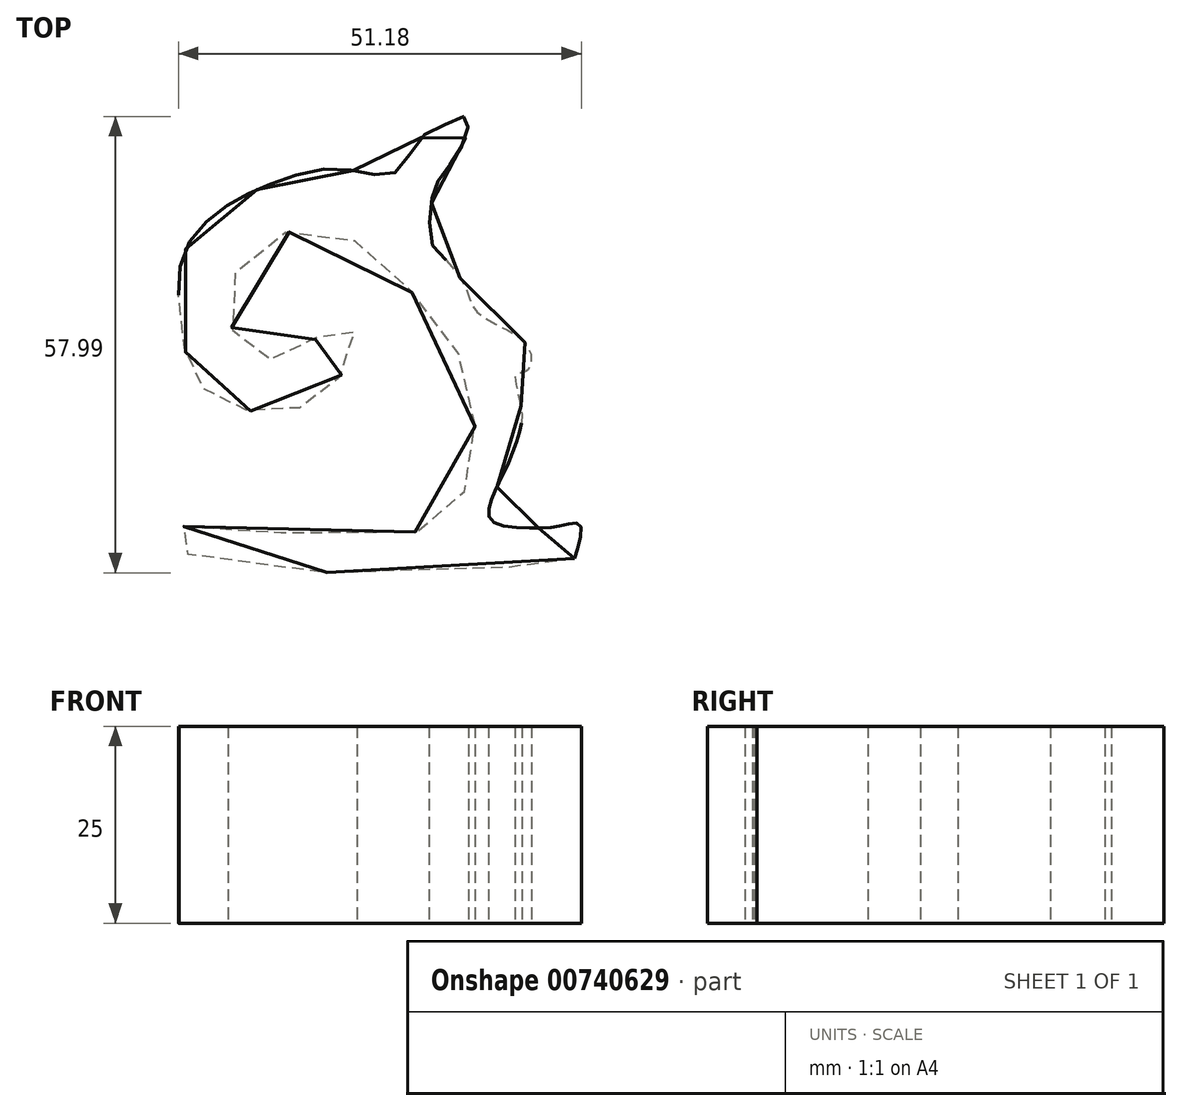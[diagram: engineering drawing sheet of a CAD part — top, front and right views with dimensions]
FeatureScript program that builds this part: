
annotation { "Feature Type Name" : "Feature", "Feature Type Description" : "" }
export const myFeature = defineFeature(function(context is Context, id is Id, definition is map)
    precondition{}
    {
        {
            var Q0;
            Q0=qCreatedBy(makeId("Top.planeOp"),FACE);
            var sketch = newSketch(context, id + "F0", { "sketchPlane" : qUnion([Q0])});
            skFitSpline(sketch, "E0", {"points": [v(124.73, -290.05) * mm, v(123.75, -290.64) * mm, v(75.1, -289.1) * mm, v(74.92, -286.08) * mm, v(74.93, -286.05) * mm, v(75.1, -285.97) * mm, v(106.34, -286.28) * mm, v(111.08, -279.96) * mm, v(111.72, -268.27) * mm, v(104.15, -256.29) * mm, v(94.37, -248.71) * mm, v(83.66, -250.92) * mm, v(80.82, -259.12) * mm, v(83.65, -263.84) * mm, v(89.62, -264.15) * mm, v(94.66, -260.06) * mm, v(97.12, -262.5) * mm, v(93.71, -268.24) * mm, v(89.3, -271.07) * mm, v(82.39, -271.07) * mm, v(77.67, -268.55) * mm, v(75.47, -264.46) * mm, v(74.53, -258.17) * mm, v(74.97, -251.62) * mm, v(78.25, -247.03) * mm, v(82.7, -244.02) * mm, v(87.1, -242.13) * mm, v(93.4, -240.56) * mm, v(98.75, -241.19) * mm, v(102.2, -240.87) * mm, v(105.04, -236.78) * mm, v(108.78, -234.71) * mm, v(111.01, -233.95) * mm, v(111.01, -236.16) * mm, v(109.44, -239.3) * mm, v(107.34, -242.18) * mm, v(106.55, -244.93) * mm, v(106.55, -249.91) * mm, v(108.65, -252.4) * mm, v(111.14, -256.2) * mm, v(112.58, -258.96) * mm, v(118.88, -263.2) * mm, v(118.56, -266.35) * mm, v(117.3, -266.67) * mm, v(117.93, -270.76) * mm, v(117.62, -274.53) * mm, v(115.73, -279.25) * mm, v(114.15, -282.68) * mm, v(114.16, -285.22) * mm, v(119.5, -286.17) * mm, v(123.28, -285.85) * mm, v(125.48, -285.85) * mm, v(124.73, -290.05) * mm]});
            skSolve(sketch);
        }
        {
            var Q0;
            Q0=makeQuery(id+"F0.imprint","IMPRINT",FACE,{"disambiguationData":[TD([[makeQuery(id+"F0.imprint","IMPRINT",EDGE,{"derivedFrom":sQuery(id+"F0.wireOp",EDGE,"E0")}),-1.0]])]});
            extrude(context, id + "F1", {"entities" : qUnion([Q0]), "depth" : 25 * mm, "offsetDistance" : 25 * mm});
        }
    });
